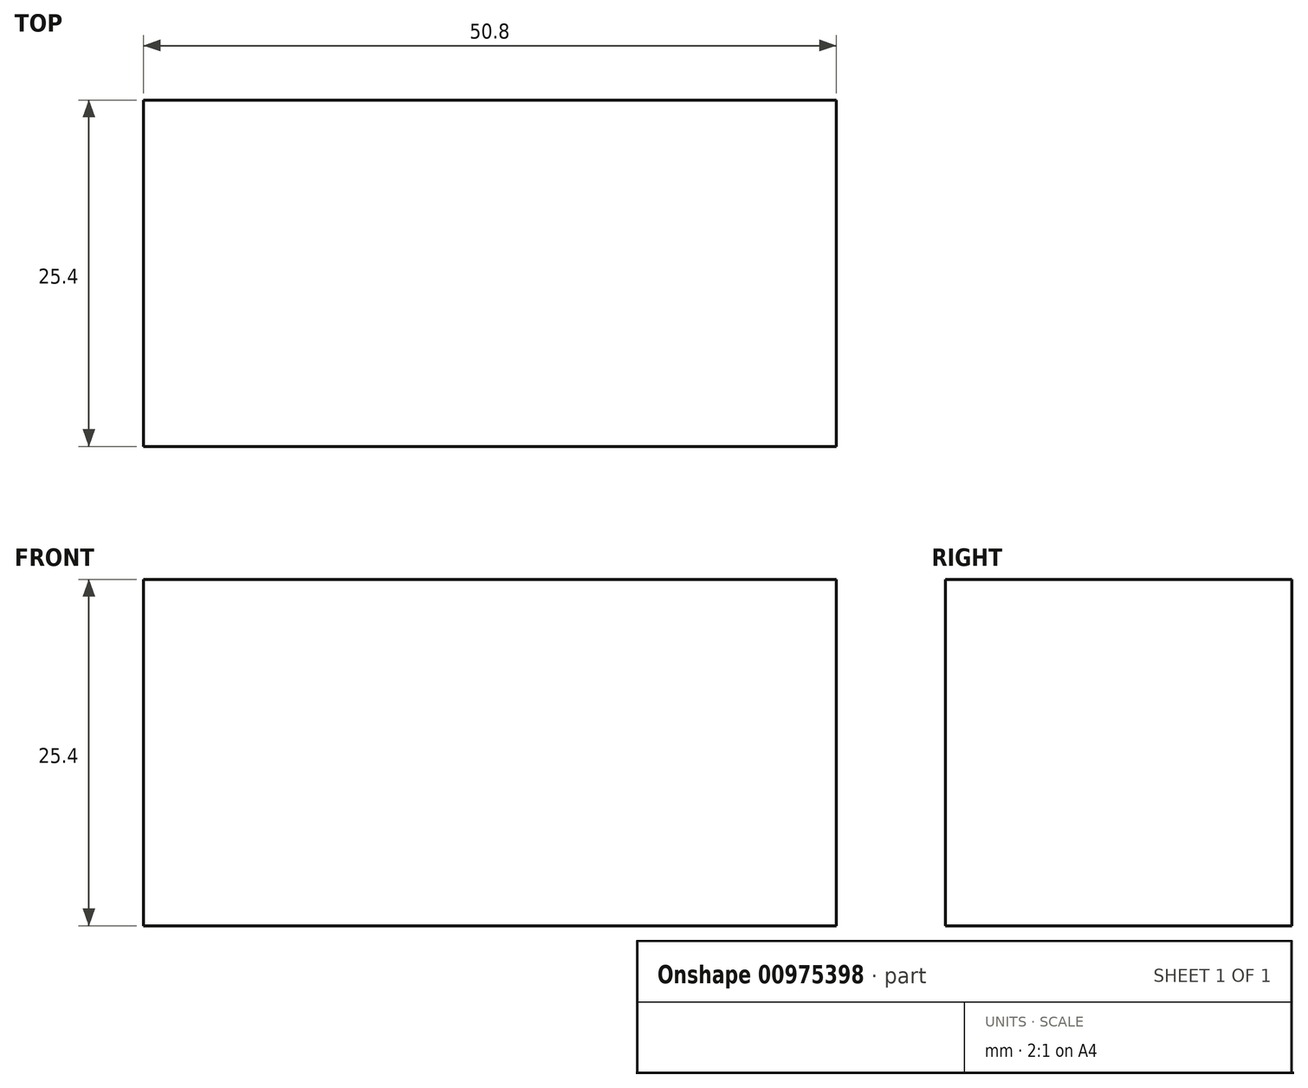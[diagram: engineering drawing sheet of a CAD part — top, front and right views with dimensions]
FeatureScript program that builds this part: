
annotation { "Feature Type Name" : "Feature", "Feature Type Description" : "" }
export const myFeature = defineFeature(function(context is Context, id is Id, definition is map)
    precondition{}
    {
        {
            var Q0;
            Q0=qCreatedBy(makeId("Top.planeOp"),FACE);
            var sketch = newSketch(context, id + "F0", { "sketchPlane" : qUnion([Q0])});
            skLineSegment(sketch, "E0.bottom", {"start": v(-23.14, 10.4) * mm, "end": v(27.66, 10.4) * mm});
            skLineSegment(sketch, "E0.top", {"start": v(-23.14, -15) * mm, "end": v(27.66, -15) * mm});
            skLineSegment(sketch, "E0.left", {"start": v(-23.14, 10.4) * mm, "end": v(-23.14, -15) * mm});
            skLineSegment(sketch, "E0.right", {"start": v(27.66, 10.4) * mm, "end": v(27.66, -15) * mm});
            skSolve(sketch);
        }
        {
            var Q0;
            Q0 = qSketchRegion(id + "F0", true);
            extrude(context, id + "F1", {"entities" : qUnion([Q0]), "depth" : 25.4 * mm, "offsetDistance" : 25.4 * mm});
        }
    });
